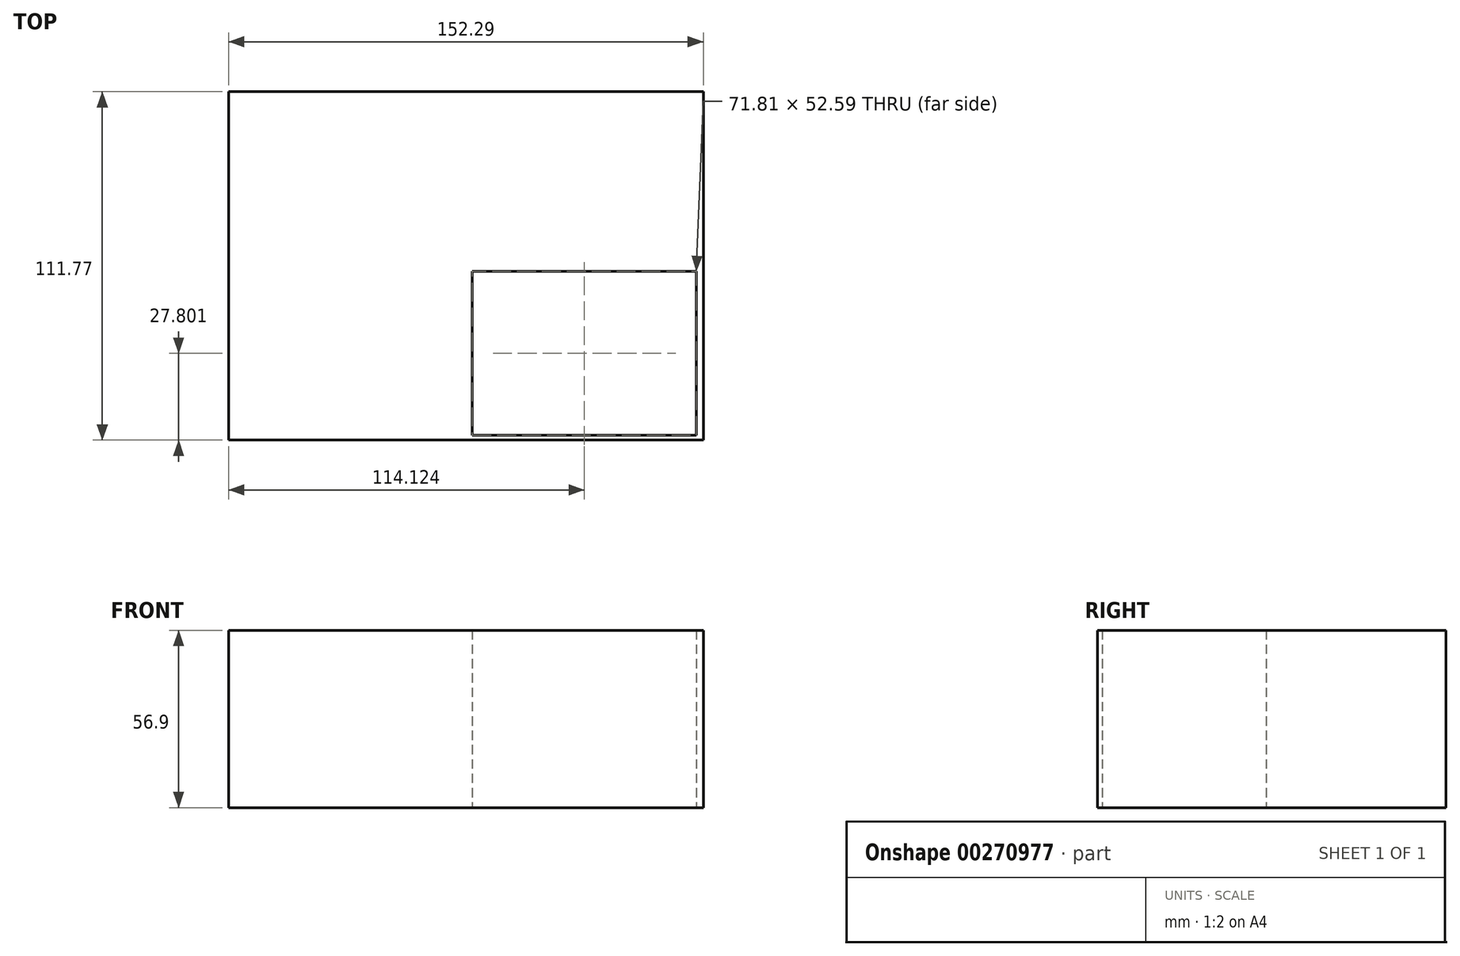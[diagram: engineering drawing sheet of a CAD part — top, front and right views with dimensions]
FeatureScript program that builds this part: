
annotation { "Feature Type Name" : "Feature", "Feature Type Description" : "" }
export const myFeature = defineFeature(function(context is Context, id is Id, definition is map)
    precondition{}
    {
        {
            var Q0;
            Q0=qCreatedBy(makeId("Top.planeOp"),FACE);
            var sketch = newSketch(context, id + "F0", { "sketchPlane" : qUnion([Q0])});
            skLineSegment(sketch, "E0.bottom", {"start": v(0, 0) * mm, "end": v(75.13, 0) * mm});
            skLineSegment(sketch, "E0.top", {"start": v(0, -75.67) * mm, "end": v(75.13, -75.67) * mm});
            skLineSegment(sketch, "E0.left", {"start": v(0, 0) * mm, "end": v(0, -75.67) * mm});
            skLineSegment(sketch, "E0.right", {"start": v(75.13, 0) * mm, "end": v(75.13, -75.67) * mm});
            skLineSegment(sketch, "E1.bottom", {"start": v(-76.22, 76.24) * mm, "end": v(75.13, 76.24) * mm});
            skLineSegment(sketch, "E1.top", {"start": v(-76.22, -75.67) * mm, "end": v(75.13, -75.67) * mm});
            skLineSegment(sketch, "E1.left", {"start": v(-76.22, 76.24) * mm, "end": v(-76.22, -75.67) * mm});
            skLineSegment(sketch, "E1.right", {"start": v(75.13, 76.24) * mm, "end": v(75.13, -75.67) * mm});
            skSolve(sketch);
        }
        {
            var Q0;
            {var subQ0=sQuery(id+"F0.wireOp",EDGE,"E0.bottom");Q0=makeQuery(id+"F0.imprint","IMPRINT",FACE,{"disambiguationData":[TD([[makeQuery(id+"F0.imprint","IMPRINT",EDGE,{"derivedFrom":subQ0}),-1.0]])]});}
            extrude(context, id + "F1", {"entities" : qUnion([Q0]), "depth" : 25.4 * mm});
        }
        {
            var Q0;
            Q0=makeQuery(id+"F1.opExtrude","SWEPT_BODY",BODY,{"disambiguationData":[OSD([sQuery(id+"F0.wireOp",EDGE,"E0.bottom"),sQuery(id+"F0.wireOp",EDGE,"E0.left"),sQuery(id+"F0.wireOp",EDGE,"E1.top"),sQuery(id+"F0.wireOp",EDGE,"E1.right")])]});
            deleteBodies(context, id + "F2", {"entities" : qUnion([Q0])});
        }
        {
            var Q0;
            Q0=qCreatedBy(makeId("Top.planeOp"),FACE);
            var sketch = newSketch(context, id + "F3", { "sketchPlane" : qUnion([Q0])});
            skLineSegment(sketch, "E2.bottom", {"start": v(-76.22, 55.32) * mm, "end": v(76.07, 55.32) * mm});
            skLineSegment(sketch, "E2.top", {"start": v(-76.22, -56.45) * mm, "end": v(76.07, -56.45) * mm});
            skLineSegment(sketch, "E2.left", {"start": v(-76.22, 55.32) * mm, "end": v(-76.22, -56.45) * mm});
            skLineSegment(sketch, "E2.right", {"start": v(76.07, 55.32) * mm, "end": v(76.07, -56.45) * mm});
            skLineSegment(sketch, "E3.bottom", {"start": v(2, -2.36) * mm, "end": v(73.8, -2.36) * mm});
            skLineSegment(sketch, "E3.top", {"start": v(2, -54.94) * mm, "end": v(73.8, -54.94) * mm});
            skLineSegment(sketch, "E3.left", {"start": v(2, -2.36) * mm, "end": v(2, -54.94) * mm});
            skLineSegment(sketch, "E3.right", {"start": v(73.8, -2.36) * mm, "end": v(73.8, -54.94) * mm});
            skSolve(sketch);
        }
        {
            var Q0;
            Q0 = qSketchRegion(id + "F3", true);
            extrude(context, id + "F4", {"entities" : qUnion([Q0]), "depth" : 56.9 * mm});
        }
    });
